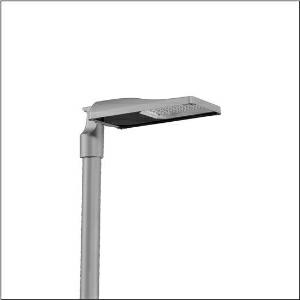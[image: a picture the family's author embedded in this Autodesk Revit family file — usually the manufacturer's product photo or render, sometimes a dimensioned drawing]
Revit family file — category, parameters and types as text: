
# Revit family: streetlight_sl_31_mini___st1_0a_5xh6d3ab08ha_9874
name_source: partatom
category: Lighting Fixtures
units: mm (PartAtom-declared; Revit-internal decimal feet)

## family parameters
Cut with Voids When Loaded = No
Host = Face
Light Source = No
Part Type = Normal
Room Calculation Point = No
Round Connector Dimension = Use Diameter
Shared = No

## types (1)
- --- (1 x LED, 9240 lm, 68.3 W, 3000K)
    Apparent Load = 68 VA
    CIE Flux Codes = 37 72 97 100 100
    Color Rendering = 70
    Color Temperature = 3000K
    Default Elevation = 1800 mm
    Description = Streetlight SL 31 mini Easy LST mast luminaire for post-top, side-entry; light control with lens of PMMA; light distribution: ST1.0a, direct asymmetric distribution, for standard-compliant lighting for roads and squares; LED: luminous flux: 9.240lm, light colour: 730, colour temperature: 3000K; luminous efficacy: 135,3lm/W; control: pre-setting: linear dimming characteristic, flexible luminous flux parameterisation, time-dependent luminous flux control, constant luminous flux control, power reduction, intelligent temperature release in ECG and LED module, overheat protection; luminaire housing, of diecast aluminium, SITECO metallic grey (DB 702S), corrosivity category C5 high according to DIN EN ISO 12944; cover of toughened safety glass, transparent, opened without tools; mast flange of diecast aluminium, SITECO metallic grey (DB 702S), spigot size: 76/60mm, mast flange included unmounted; cable length: 8,5m, connection cable pre-assembled; mains connection: 220..240V, AC, 50/60Hz; power consumption (at start of service life): 68,3W / (at end of service life): 74,8W / (with reduced operation 50%): 29,7W; protection rating (complete): IP66; insulation class (complete): insulation class II (safety insulation); impact resistance: IK10; certification: CE, ENEC, ENEC+, VDE, UKCA; permissible operating ambient temperature for outdoor applications: -40..+50°C; packaging unit: 1 piece

Light Distribution: ST1.0a
    Height = 76 mm
    Lamp = 1 x LED
    Lamp Light Flux = 9240 lm
    Lamp Power = 68.3 W
    Lamp count = 1
    Length = 547 mm
    Luminous efficacy = 135 lm/W
    Manufacturer = Siteco
    ModVariant = No
    Model = 5XH6D3AB08HA
    Number of Poles = 1
    OnlyDefault = Yes
    Power Factor = 1
    Product Name = Streetlight SL 31 mini | ST1.0a
    Product group = mast luminaire | pylon top
    ProductGroupID = 6100
    Protection Class = Protection class II
    Protection Degree = IP 66
    RLX_Detail_Level = 1
    RLX_Emergency_Light_Flux = 0 lm
    RLX_Emergency_Type = 0
    RLX_Emergency_Type_DB = No
    RlxData = <blob elided: 39457 chars, md5=5d33c9ad>
    Socket = socket
    Standby Power = 0 W
    System Light Flux = 9240 lm
    System Power = 68 W
    Type Comments = factory setting: luminous flux: 100 % | dim-lin: 254 | 693 mA
    Type Image = l_1300326.jpg
    URL = http://relux.com
    VarID = @adj_060825
    Voltage = 0 V
    Weight = 0.00 kg
    Width = 265 mm

## geometry (parser evidence)
native form markers: Blend x4, Sweep x10
no freeform markers — native parametric forms only
